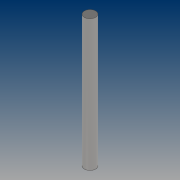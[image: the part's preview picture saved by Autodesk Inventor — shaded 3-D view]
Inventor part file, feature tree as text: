
AUTODESK INVENTOR PART (.ipt)
format: ipt  version: 2021 (Build 250183000, 183)  size: 75,264 bytes
history: native  units: mm
features: extrude x1, sketch x1
ambient origin geometry x8: Origin, YZ Plane, XZ Plane, XY Plane, X Axis, Y Axis, Z Axis, Center Point
bodies: Solid1 (feature_tree)
feature tree (2):
  extrude  "Extrusion1"  Depth=70.0mm TaperAngle=0.0deg
  sketch  "Sketch1"  dims[d0=6.0mm d1=70.0mm d2=0.0mm]
